# Revit family: xCFLED_Hosted_R16_V1.0
name_source: partatom
category: Lighting Fixtures
revit_build: Autodesk Revit 2016 (Build: 20150220_1215(x64)
units: mm (PartAtom-declared; Revit-internal decimal feet)

## family parameters
Cut with Voids When Loaded = No
Host = Face
Light Source = Yes
Part Type = Normal
Room Calculation Point = No
Round Connector Dimension = Use Diameter
Shared = No

## types (9) — shared parameters
Annotation Direction = Exit_Annotation : Double Sided Direction Exit Luminaire
Apparent Load = 4 W
Ballast = Electronic
Charging Method = Intelligent current limited constant voltage
Color Filter = 16777215
Construction = ABS Body and Diffuser with clear tamper proof cover
Default Elevation = 1219 mm
Diffuser = All directional inserts included in the box
Dimming Lamp Color Temperature Shift = <None>
Double Sided = Yes
Emit Shape Visible in Rendering = No
Emit from Rectangle Length = 1219 mm
Emit from Rectangle Width = 610 mm
Height = 215 mm
IP Rating = IP20
Length = 355 mm
Manufacturer = Clevertronics
Mounting = Wall, Ceiling Single-Sided & Ceiling Double-Sided
Operating Mode = Maintained
Operating Temperature = 1C to 40C
Operating Voltage = 240 V
Sign Direction = Sign : Exit
Single Sided = Yes
Tilt Angle = -90.00°
Viewing Distance = 24000 mm  [stored 78.7402 ft]
Wattage Comments = Standby
Width = 80 mm  [stored 0.262467 ft]

## per-type parameters (varying)
| type | AS2293 | Battery | Description | Lamp | Photometric Web File | Power Consumption | Power Consumption (max) | Testing System | Weight |
| ECFLED-LI | C0=E2.5 C90=E2 | Lithium Iron Phosphate, 3.2V 600mAh | Economy Lithium Cleverfit Emergency Exit | 4 x LED 100,000hour | ll20037_ECFLED-LI.IES | 1 W | 2.0W | Manual Test Switch | 1.2kg |
| CCFLED | C0=E2.5 C90=E2 | Lithium Iron Phosphate, 3.2V 1500mAh | LP Premium Cleverfit Emergency Exit, Enabled with Clevertest Plus | 6 x LED 100,000hour | ll21444 -  CCFLED-ZW Gen2 .IES | 3 W | 5.1W | Clevertest Plus Enabled (not activated by default) | 1.8kg |
| CCFLED-CT | C0=E2.5 C90=E2 | Lithium Iron Phosphate, 3.2V 1500mAh | LP Premium Cleverfit Emergency Exit | 6 x LED 100,000hour | ll21444 -  CCFLED-ZW Gen2 .IES | 3 W | 5.1W | Clevertest | 1.8kg |
| CCFLED-ZW | C0=E2.5 C90=E2 | Lithium Iron Phosphate, 3.2V 1500mAh | LP Premium Cleverfit Emergency Exit | 6 x LED 100,000hour | ll21444 -  CCFLED-ZW Gen2 .IES | 3 W | 5.1W | Zoneworks Computerised Testing | 1.8kg |
| CCFLED-DALI | C0=E2.5 C90=E2 | Lithium Iron Phosphate, 3.2V 1500mAh | LP Premium Cleverfit Emergency Exit | 6 x LED 100,000hour | ll21444 -  CCFLED-ZW Gen2 .IES | 3 W | 5.1W | DALI Registered | 1.8kg |
| LCFLED | C0=E2 C90=E2 | Lithium Nanophosphate, 3.2V 2500mAh | L10 Lithium Nonophosphate Cleverfit Emergency Exit, Enabled with Clevertest Plus | 6 x LED 100,000hour | ll16167 - LCFLED.IES | 3 W | 4.5W | Clevertest Plus Enabled (not activated by default) | 1.8kg |
| LCFLED-CT | C0=E2 C90=E2 | Lithium Nonphosphate, 3.2V 2500mAh | L10 Optimum Cleverfit Emergency Exit | 6 x LED 100,000hour | ll16167 - LCFLED.IES | 3 W | 5.1W | Clevertest | 1.8kg |
| LCFLED-ZW | C0=E2 C90=E2 | Lithium Nanophosphate, 3.2V 2500mAh | L10 Lithium Nonophosphate Cleverfit Emergency Exit | 6 x LED 100,000hour | ll16167 - LCFLED.IES | 3 W | 4.5W | Zoneworks Computerised Testing | 1.8kg |
| LCFLED-DALI | C0=E2 C90=E2 | Lithium Nanophosphate, 3.2V 2500mAh | L10 Lithium Nonophosphate Cleverfit Emergency Exit | 6 x LED 100,000hour | ll16167 - LCFLED.IES | 3 W | 4.7W | DALI Compatible | 1.8kg |

note: column(s) folded — value = type name in every type: Model

note: [stored X ft] marks values corroborated as IEEE doubles in the binary element streams (Revit-internal decimal feet)

## geometry (parser evidence)
native form markers: Sweep x8
no freeform markers — native parametric forms only
